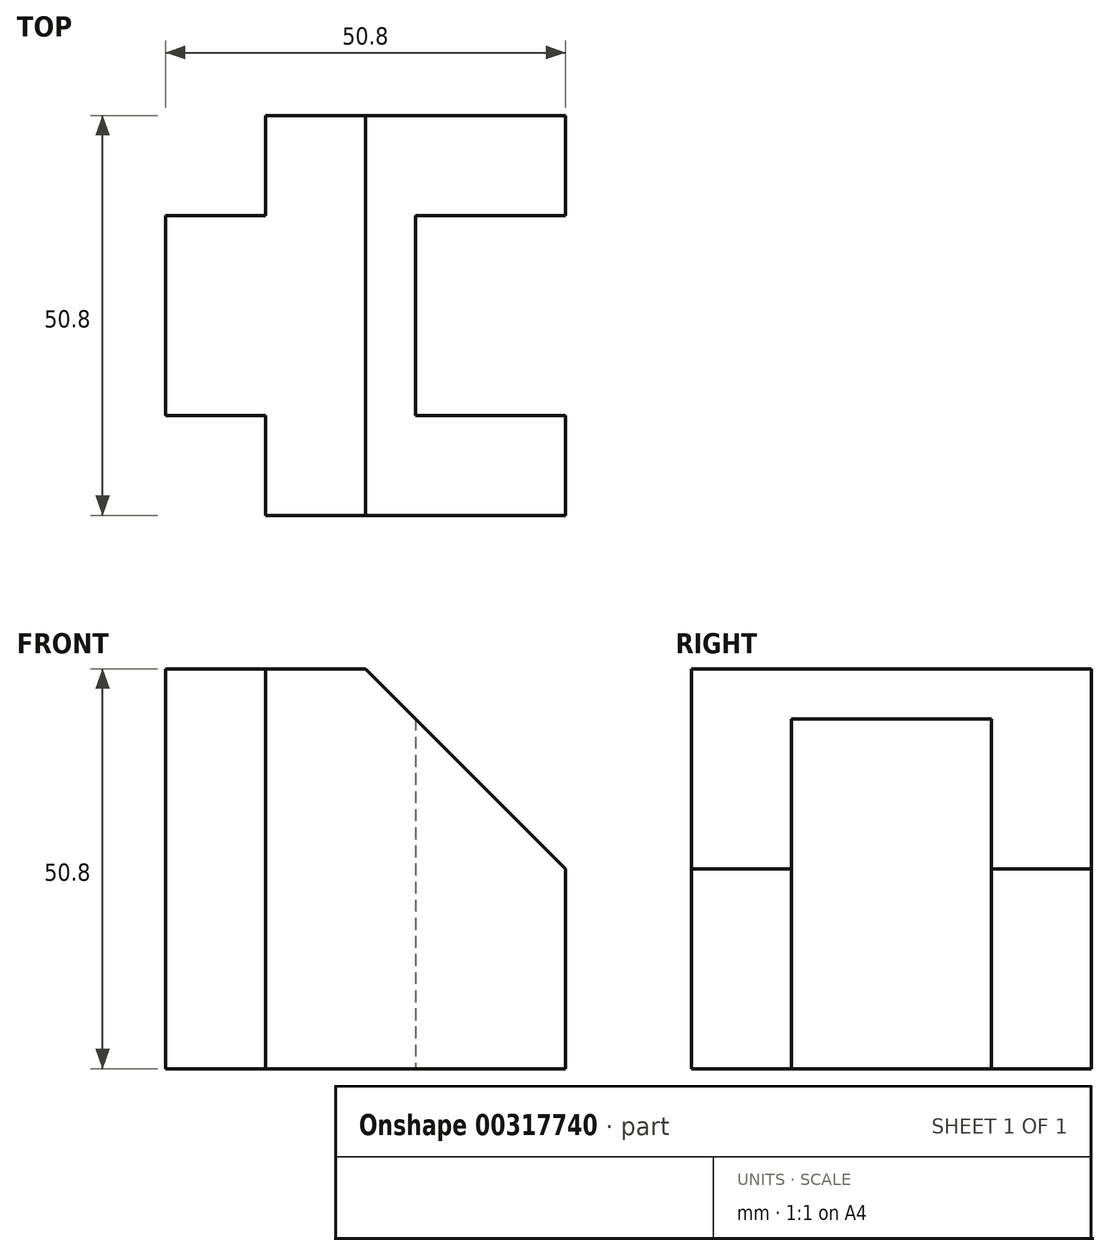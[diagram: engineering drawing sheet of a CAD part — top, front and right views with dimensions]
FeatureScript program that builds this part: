
annotation { "Feature Type Name" : "Feature", "Feature Type Description" : "" }
export const myFeature = defineFeature(function(context is Context, id is Id, definition is map)
    precondition{}
    {
        {
            var Q0;
            Q0=qCreatedBy(makeId("Front.planeOp"),FACE);
            var sketch = newSketch(context, id + "F0", { "sketchPlane" : qUnion([Q0])});
            skLineSegment(sketch, "E0.bottom", {"start": v(0, 0) * mm, "end": v(12.7, 0) * mm});
            skLineSegment(sketch, "E0.top", {"start": v(0, 50.8) * mm, "end": v(12.7, 50.8) * mm});
            skLineSegment(sketch, "E0.left", {"start": v(0, 0) * mm, "end": v(0, 50.8) * mm});
            skLineSegment(sketch, "E1.bottom", {"start": v(12.7, 0) * mm, "end": v(50.8, 0) * mm});
            skLineSegment(sketch, "E1.right", {"start": v(50.8, 0) * mm, "end": v(50.8, 25.4) * mm});
            skLineSegment(sketch, "E2.bottom", {"start": v(12.7, 50.8) * mm, "end": v(25.4, 50.8) * mm});
            skLineSegment(sketch, "E3", {"start": v(25.4, 50.8) * mm, "end": v(50.8, 25.4) * mm});
            skLineSegment(sketch, "E4", {"start": v(12.7, 50.8) * mm, "end": v(12.7, 0) * mm});
            skSolve(sketch);
        }
        {
            var Q0;
            Q0 = qSketchRegion(id + "F0", true);
            extrude(context, id + "F1", {"entities" : qUnion([Q0]), "endBound" : BoundingType.SYMMETRIC, "depth" : 50.8 * mm});
        }
        {
            var Q0;
            Q0=makeQuery(id+"F1.opExtrude","SWEPT_FACE",FACE,{"disambiguationData":[OSD([sQuery(id+"F0.wireOp",EDGE,"E0.top"),sQuery(id+"F0.wireOp",EDGE,"E2.bottom")])]});
            var sketch = newSketch(context, id + "F2", { "sketchPlane" : qUnion([Q0])});
            skLineSegment(sketch, "E5.bottom", {"start": v(12.7, 12.7) * mm, "end": v(0, 12.7) * mm});
            skLineSegment(sketch, "E5.top", {"start": v(12.7, -12.7) * mm, "end": v(0, -12.7) * mm});
            skPoint(sketch, "E5.middle", {"position": v(0, 0) * mm});
            skPoint(sketch, "E6", {"position": v(0, 12.7) * mm});
            skPoint(sketch, "E7", {"position": v(0, -12.7) * mm});
            skLineSegment(sketch, "E8", {"start": v(12.7, 12.7) * mm, "end": v(12.7, 25.4) * mm});
            skLineSegment(sketch, "E9", {"start": v(12.7, -12.7) * mm, "end": v(12.7, -25.4) * mm});
            skSolve(sketch);
        }
        {
            var Q0;
            {var subQ0=sQuery(id+"F2.wireOp",EDGE,"E5.bottom");Q0=makeQuery(id+"F2.imprint","IMPRINT",FACE,{"disambiguationData":[TD([[makeQuery(id+"F2.imprint","IMPRINT",EDGE,{"derivedFrom":subQ0}),-1.0]])]});}
            var Q1;
            {var subQ0=sQuery(id+"F2.wireOp",EDGE,"E5.top");Q1=makeQuery(id+"F2.imprint","IMPRINT",FACE,{"disambiguationData":[TD([[makeQuery(id+"F2.imprint","IMPRINT",EDGE,{"derivedFrom":subQ0}),1.0]])]});}
            extrude(context, id + "F3", {"entities" : qUnion([Q0, Q1]), "operationType" : NewBodyOperationType.REMOVE, "endBound" : BoundingType.THROUGH_ALL, "oppositeDirection" : true, "depth" : 25.4 * mm});
        }
        {
            var Q0;
            Q0=makeQuery(id+"F1.opExtrude","SWEPT_FACE",FACE,{"disambiguationData":[OSD([sQuery(id+"F0.wireOp",EDGE,"E0.bottom"),sQuery(id+"F0.wireOp",EDGE,"E1.bottom")])]});
            var sketch = newSketch(context, id + "F4", { "sketchPlane" : qUnion([Q0])});
            skPoint(sketch, "E10", {"position": v(31.75, 12.7) * mm});
            skPoint(sketch, "E11", {"position": v(31.75, -12.7) * mm});
            skLineSegment(sketch, "E12.bottom", {"start": v(50.8, 12.7) * mm, "end": v(31.75, 12.7) * mm});
            skLineSegment(sketch, "E12.top", {"start": v(50.8, -12.7) * mm, "end": v(31.75, -12.7) * mm});
            skLineSegment(sketch, "E12.left", {"start": v(50.8, 12.7) * mm, "end": v(50.8, -12.7) * mm});
            skLineSegment(sketch, "E12.right", {"start": v(31.75, 12.7) * mm, "end": v(31.75, -12.7) * mm});
            skSolve(sketch);
        }
        {
            var Q0;
            Q0=makeQuery(id+"F4.imprint","IMPRINT",FACE,{"disambiguationData":[TD([[makeQuery(id+"F4.imprint","IMPRINT",EDGE,{"derivedFrom":sQuery(id+"F4.wireOp",EDGE,"E12.bottom")}),1.0]])]});
            extrude(context, id + "F5", {"entities" : qUnion([Q0]), "operationType" : NewBodyOperationType.REMOVE, "endBound" : BoundingType.THROUGH_ALL, "oppositeDirection" : true, "depth" : 25.4 * mm});
        }
    });
